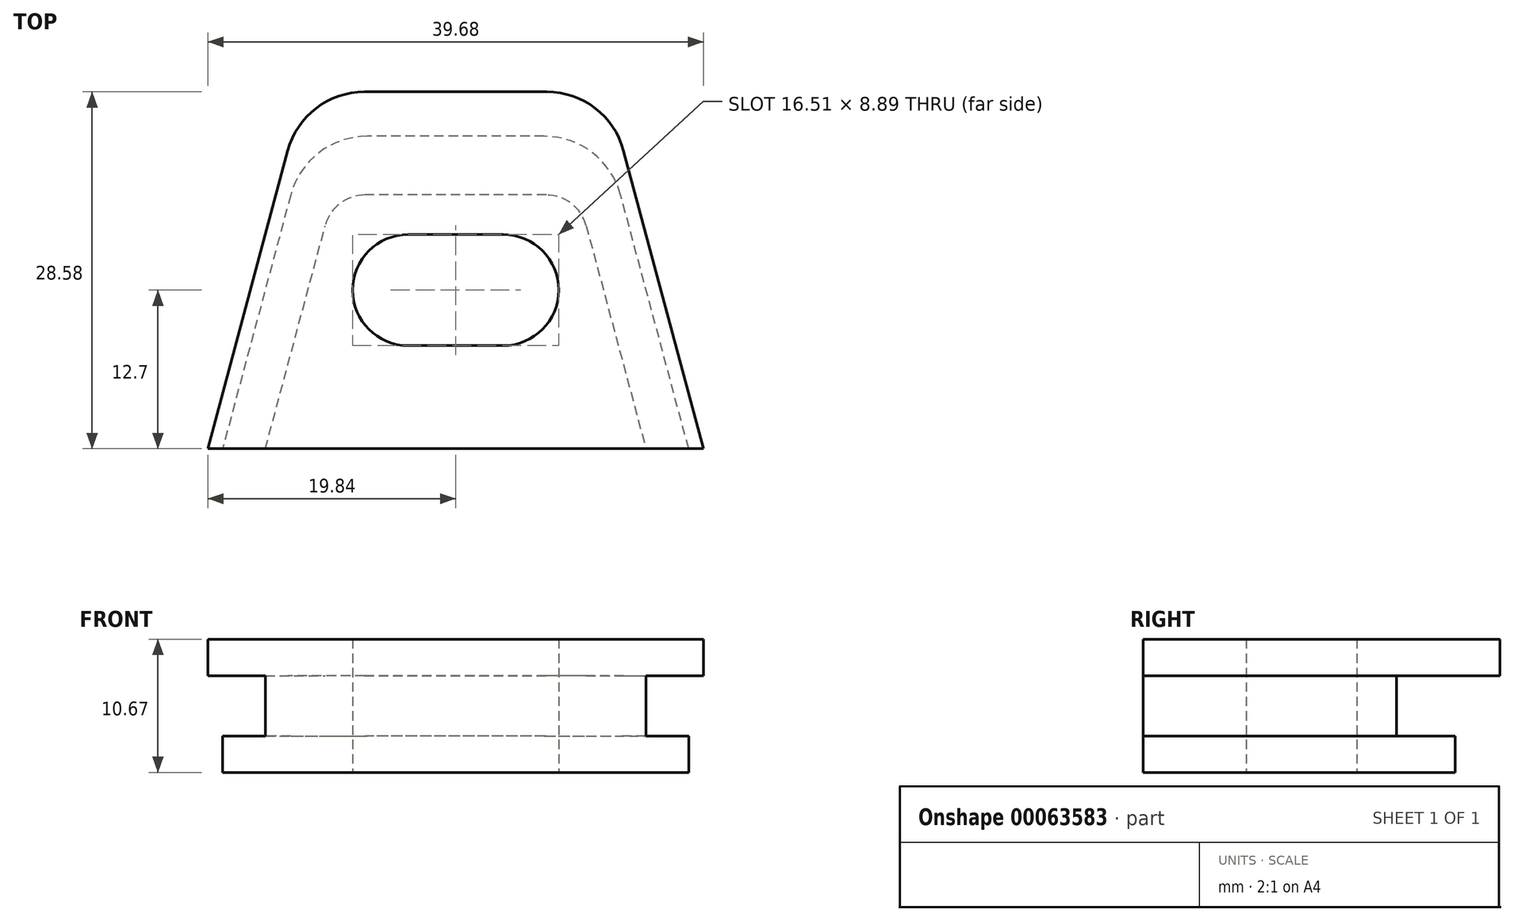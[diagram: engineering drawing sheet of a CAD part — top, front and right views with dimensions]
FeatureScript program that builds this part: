
annotation { "Feature Type Name" : "Feature", "Feature Type Description" : "" }
export const myFeature = defineFeature(function(context is Context, id is Id, definition is map)
    precondition{}
    {
        {
            var Q0;
            Q0=qCreatedBy(makeId("Top.planeOp"),FACE);
            var sketch = newSketch(context, id + "F0", { "sketchPlane" : qUnion([Q0])});
            skLineSegment(sketch, "E0", {"start": v(-15.24, 0) * mm, "end": v(15.24, 0) * mm});
            skLineSegment(sketch, "E1", {"start": v(-15.24, 0) * mm, "end": v(-9.8, 20.32) * mm});
            skLineSegment(sketch, "E2", {"start": v(9.8, 20.32) * mm, "end": v(-9.8, 20.32) * mm});
            skLineSegment(sketch, "E3", {"start": v(9.8, 20.32) * mm, "end": v(15.24, 0) * mm});
            skSolve(sketch);
        }
        {
            var Q0;
            Q0=makeQuery(id+"F0.imprint","IMPRINT",FACE,{"disambiguationData":[TD([[makeQuery(id+"F0.imprint","IMPRINT",EDGE,{"derivedFrom":sQuery(id+"F0.wireOp",EDGE,"E0")}),1.0]])]});
            extrude(context, id + "F1", {"entities" : qUnion([Q0]), "depth" : 4.83 * mm});
        }
        {
            var Q0;
            Q0=makeQuery(id+"F1.opExtrude","CAP_FACE",FACE,{"disambiguationData":[OSD([sQuery(id+"F0.wireOp",EDGE,"E0"),sQuery(id+"F0.wireOp",EDGE,"E1"),sQuery(id+"F0.wireOp",EDGE,"E2"),sQuery(id+"F0.wireOp",EDGE,"E3")])],"isStart":false});
            var sketch = newSketch(context, id + "F2", { "sketchPlane" : qUnion([Q0])});
            skLineSegment(sketch, "E4", {"start": v(19.84, 0) * mm, "end": v(-19.84, 0) * mm});
            skPoint(sketch, "E4.startSnap0", {"position": v(0, 0) * mm});
            skPoint(sketch, "E4.endSnap0", {"position": v(0, 0) * mm});
            skLineSegment(sketch, "E5", {"start": v(-19.84, 0) * mm, "end": v(-12.19, 28.58) * mm});
            skLineSegment(sketch, "E6", {"start": v(-12.19, 28.58) * mm, "end": v(12.19, 28.58) * mm});
            skLineSegment(sketch, "E7", {"start": v(12.19, 28.58) * mm, "end": v(19.84, 0) * mm});
            skSolve(sketch);
        }
        {
            var Q0;
            Q0 = qSketchRegion(id + "F2", true);
            extrude(context, id + "F3", {"entities" : qUnion([Q0]), "operationType" : NewBodyOperationType.ADD, "depth" : 2.92 * mm});
        }
        {
            var Q0;
            Q0=makeQuery(id+"F1.opExtrude","CAP_FACE",FACE,{"disambiguationData":[OSD([sQuery(id+"F0.wireOp",EDGE,"E0"),sQuery(id+"F0.wireOp",EDGE,"E1"),sQuery(id+"F0.wireOp",EDGE,"E2"),sQuery(id+"F0.wireOp",EDGE,"E3")])],"isStart":true});
            var sketch = newSketch(context, id + "F4", { "sketchPlane" : qUnion([Q0])});
            skLineSegment(sketch, "E8", {"start": v(-18.66, 0) * mm, "end": v(18.66, 0) * mm});
            skLineSegment(sketch, "E9", {"start": v(18.66, 0) * mm, "end": v(11.95, -25.02) * mm});
            skLineSegment(sketch, "E10", {"start": v(11.95, -25.02) * mm, "end": v(-11.95, -25.02) * mm});
            skLineSegment(sketch, "E11", {"start": v(-11.95, -25.02) * mm, "end": v(-18.66, 0) * mm});
            skSolve(sketch);
        }
        {
            var Q0;
            Q0 = qSketchRegion(id + "F4", true);
            extrude(context, id + "F5", {"entities" : qUnion([Q0]), "operationType" : NewBodyOperationType.ADD, "depth" : 2.92 * mm});
        }
        {
            var Q0;
            Q0=makeQuery(id+"F5.opExtrude","CAP_FACE",FACE,{"disambiguationData":[OSD([sQuery(id+"F4.wireOp",EDGE,"E8"),sQuery(id+"F4.wireOp",EDGE,"E9"),sQuery(id+"F4.wireOp",EDGE,"E10"),sQuery(id+"F4.wireOp",EDGE,"E11")])],"isStart":false});
            var sketch = newSketch(context, id + "F6", { "sketchPlane" : qUnion([Q0])});
            skArc(sketch, "E12", {"start": v(-3.8, -8.26) * mm, "mid": v(-8.25, -12.7) * mm, "end": v(-3.8, -17.14) * mm});
            skArc(sketch, "E13", {"start": v(3.8, -17.14) * mm, "mid": v(8.25, -12.7) * mm, "end": v(3.8, -8.26) * mm});
            skLineSegment(sketch, "E14", {"start": v(-3.8, -8.26) * mm, "end": v(3.8, -8.26) * mm});
            skLineSegment(sketch, "E15", {"start": v(-3.8, -17.14) * mm, "end": v(3.8, -17.14) * mm});
            skPoint(sketch, "E16", {"position": v(0, -8.26) * mm});
            skSolve(sketch);
        }
        {
            var Q0;
            Q0 = qSketchRegion(id + "F6", true);
            extrude(context, id + "F7", {"entities" : qUnion([Q0]), "operationType" : NewBodyOperationType.REMOVE, "oppositeDirection" : true, "depth" : 25.4 * mm});
        }
        {
            var Q0;
            Q0=makeQuery(id+"F1.opExtrude","SWEPT_EDGE",EDGE,{"disambiguationData":[OSD([sQuery(id+"F0.wireOp",EDGE,"E2"),sQuery(id+"F0.wireOp",EDGE,"E3")])]});
            var Q1;
            Q1=makeQuery(id+"F1.opExtrude","SWEPT_EDGE",EDGE,{"disambiguationData":[OSD([sQuery(id+"F0.wireOp",EDGE,"E1"),sQuery(id+"F0.wireOp",EDGE,"E2")])]});
            fillet(context, id + "F8", {"entities" : qUnion([Q0, Q1]), "radius" : 3.3 * mm, "tangentPropagation" : true, "allowEdgeOverflow" : false});
        }
        {
            var Q0;
            Q0=makeQuery(id+"F3.opExtrude","SWEPT_EDGE",EDGE,{"disambiguationData":[OSD([sQuery(id+"F2.wireOp",EDGE,"E6"),sQuery(id+"F2.wireOp",EDGE,"E7")])]});
            var Q1;
            Q1=makeQuery(id+"F3.opExtrude","SWEPT_EDGE",EDGE,{"disambiguationData":[OSD([sQuery(id+"F2.wireOp",EDGE,"E5"),sQuery(id+"F2.wireOp",EDGE,"E6")])]});
            var Q2;
            Q2=makeQuery(id+"F5.opExtrude","SWEPT_EDGE",EDGE,{"disambiguationData":[OSD([sQuery(id+"F4.wireOp",EDGE,"E9"),sQuery(id+"F4.wireOp",EDGE,"E10")])]});
            var Q3;
            Q3=makeQuery(id+"F5.opExtrude","SWEPT_EDGE",EDGE,{"disambiguationData":[OSD([sQuery(id+"F4.wireOp",EDGE,"E10"),sQuery(id+"F4.wireOp",EDGE,"E11")])]});
            fillet(context, id + "F9", {"entities" : qUnion([Q0, Q1, Q2, Q3]), "radius" : 6.35 * mm, "tangentPropagation" : true, "allowEdgeOverflow" : false});
        }
    });
